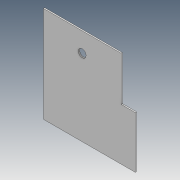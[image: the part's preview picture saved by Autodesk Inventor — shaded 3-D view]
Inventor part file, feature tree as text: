
AUTODESK INVENTOR PART (.ipt)
format: ipt  version: 2021 (Build 250183000, 183)  size: 108,032 bytes
history: native  units: in
note: dims shown in document units (in); Inventor stores cm internally (conversion verified against a paired STEP export)
features: extrude x4, sketch x4, other x1
ambient origin geometry x8: Origin, YZ Plane, XZ Plane, XY Plane, X Axis, Y Axis, Z Axis, Center Point
bodies: Body1 (feature_tree)
feature tree (9):
  other  "Sólido1"
  extrude  "Extrusão1"  Depth=1.1811in
  extrude  "Extrusão2"  Depth=0.0197in
  extrude  "Extrusão3"  Depth=0.0197in TaperAngle=0.0deg
  extrude  "Extrusão4"  Depth=0.0197in TaperAngle=0.0deg
  sketch  "Esboço1"  dims[d0=1.1811in d1=1.4331in]
  sketch  "Esboço2"  dims[d2=0.0197in d3=0.0in d4=0.2953in]
  sketch  "Esboço4"  dims[d5=0.1181in d6=0.0197in d7=0.0in]
  sketch  "Esboço5"  dims[d10=0.0276in d11=0.0197in d12=0.0in d13=0.1575in d14=0.1575in d15=0.2165in d16=0.7874in d17=0.0197in d18=0.0in]
